# Revit family: TRIM_HARDIE_ADJUSTABLE LENGTH
name_source: partatom
category: Generic Models
units: mm (PartAtom-declared; Revit-internal decimal feet)

## family parameters
Can host rebar = No
Cut with Voids When Loaded = Yes
Part Type = Normal
Room Calculation Point = No
Round Connector Dimension = Use Diameter
Shared = No

## types (7) — shared parameters
Default Elevation = 0' - 0"

## per-type parameters (varying)
| type | Dim_THICKNESS | Dim_TRIM WIDTH | Mat_HARDIE TRIM |
| 1" X 4 1/2" | 0' - 1" | 0' - 4 1/2" | MATERIAL_HARDIE BOARD |
| 1" X 3 1/2" | 0' - 1" | 0' - 3 1/2" | MATERIAL_HARDIE BOARD |
| 3/4" X 2 1/2"_BATTEN | 0' - 0 3/4" | 0' - 2 1/2" | MATERIALS_HARDIE PANEL (SMOOTH BOOTHBAY) |
| 1" X 5 1/2" | 0' - 1" | 0' - 5 1/2" | MATERIAL_HARDIE BOARD |
| 1" X 7 1/4" | 0' - 1" | 0' - 7 1/4" | MATERIAL_HARDIE BOARD |
| 1" X 11 1/4" | 0' - 1" | 0' - 11 1/4" | MATERIAL_HARDIE BOARD |
| 1" X 9 1/4" | 0' - 1" | 0' - 7 1/4" | MATERIAL_HARDIE BOARD |

## geometry (parser evidence)
native form markers: Sweep x1
no freeform markers — native parametric forms only
